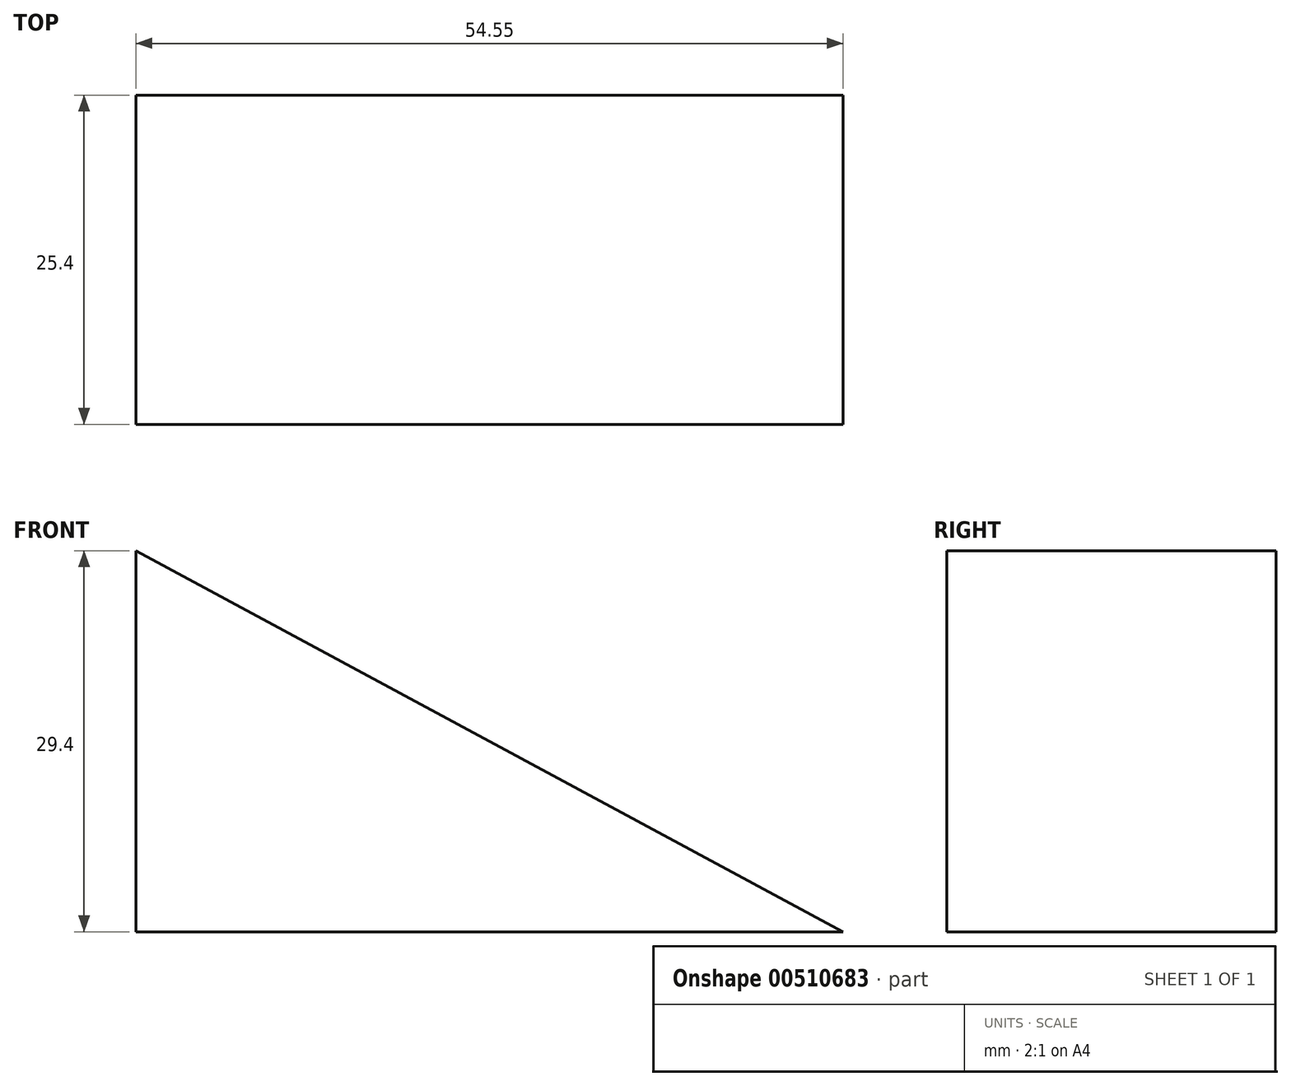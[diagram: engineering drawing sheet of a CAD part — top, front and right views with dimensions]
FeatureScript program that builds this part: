
annotation { "Feature Type Name" : "Feature", "Feature Type Description" : "" }
export const myFeature = defineFeature(function(context is Context, id is Id, definition is map)
    precondition{}
    {
        {
            var Q0;
            Q0=qCreatedBy(makeId("Front.planeOp"),FACE);
            var sketch = newSketch(context, id + "F0", { "sketchPlane" : qUnion([Q0])});
            skLineSegment(sketch, "E0", {"start": v(-20.98, 0) * mm, "end": v(-20.98, 29.4) * mm});
            skLineSegment(sketch, "E1", {"start": v(-20.98, 0) * mm, "end": v(33.57, 0) * mm});
            skLineSegment(sketch, "E2", {"start": v(33.57, 0) * mm, "end": v(-20.98, 29.4) * mm});
            skSolve(sketch);
        }
        {
            var Q0;
            Q0 = qSketchRegion(id + "F0", true);
            extrude(context, id + "F1", {"entities" : qUnion([Q0]), "depth" : 25.4 * mm});
        }
    });
